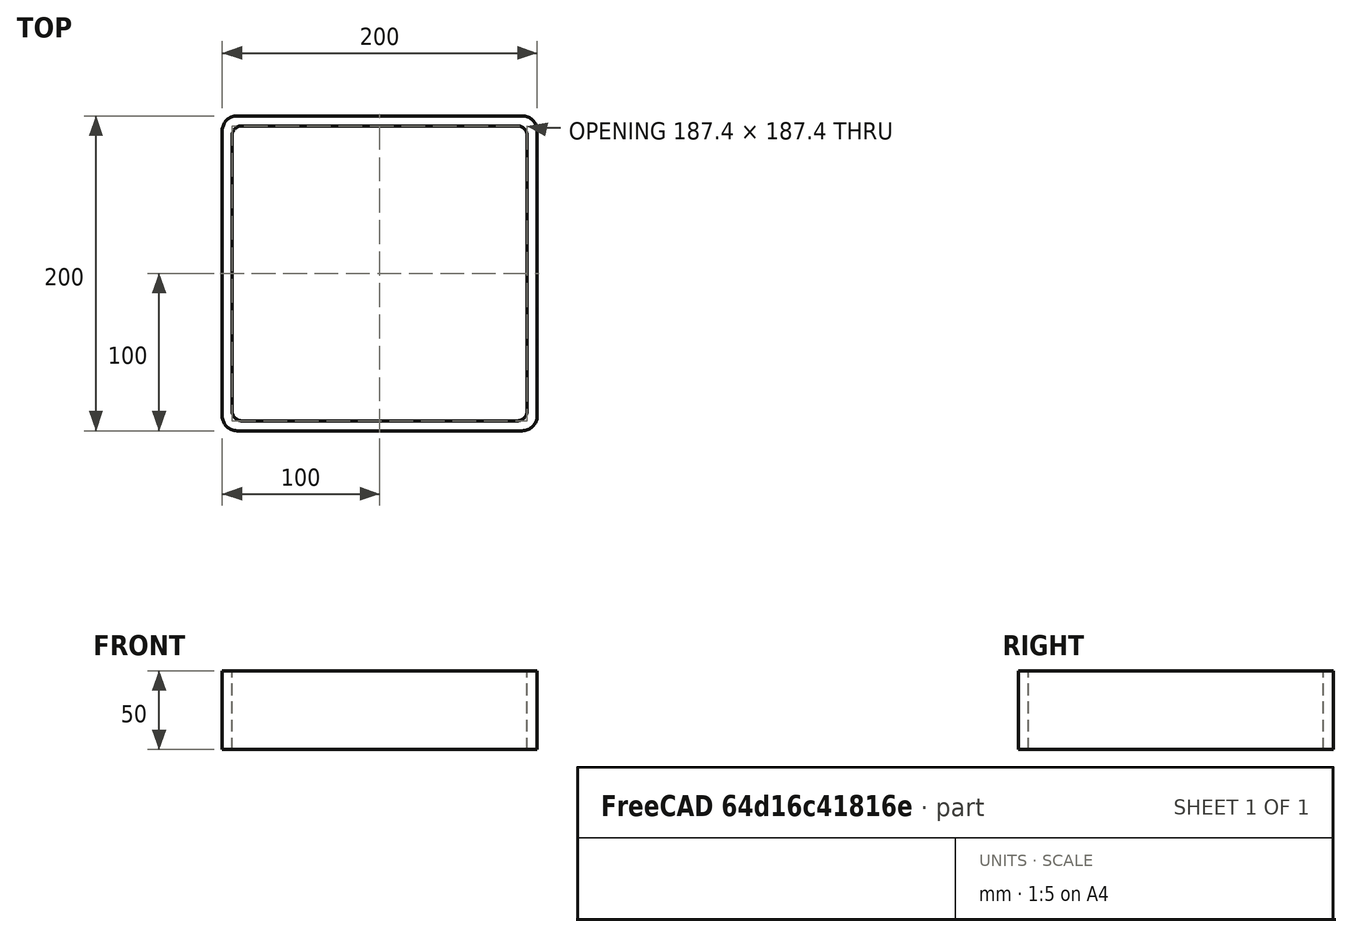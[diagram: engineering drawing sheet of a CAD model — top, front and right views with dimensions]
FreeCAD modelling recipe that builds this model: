
FCSTD DOCUMENT  (FreeCAD 0.15R4671 (Git))
Label: Square hollow section 200x200x6.3 EN10219 S235JRH
License: All rights reserved
LicenseURL: http://en.wikipedia.org/wiki/All_rights_reserved
objects: Sketcher::SketchObject×1, Part::Extrusion×1
note: 2 computed .brp shape members not serialized (recipe doc carries the construction recipe); baked Part::Feature solids carry a one-line shape summary decoded from their .brp

FEATURE [Sketcher::SketchObject] Sketch
  sketch-geometry (16):
    g0: LineSegment StartX=-87.4 StartY=93.7 StartZ=0 EndX=87.4 EndY=93.7 EndZ=0
    g1: LineSegment StartX=93.7 StartY=87.4 StartZ=0 EndX=93.7 EndY=-87.4 EndZ=0
    g2: LineSegment StartX=87.4 StartY=-93.7 StartZ=0 EndX=-87.4 EndY=-93.7 EndZ=0
    g3: LineSegment StartX=-93.7 StartY=-87.4 StartZ=0 EndX=-93.7 EndY=87.4 EndZ=0
    g4: LineSegment StartX=-90.55 StartY=100 StartZ=0 EndX=90.55 EndY=100 EndZ=0
    g5: LineSegment StartX=100 StartY=90.55 StartZ=0 EndX=100 EndY=-90.55 EndZ=0
    g6: LineSegment StartX=90.55 StartY=-100 StartZ=0 EndX=-90.55 EndY=-100 EndZ=0
    g7: LineSegment StartX=-100 StartY=-90.55 StartZ=0 EndX=-100 EndY=90.55 EndZ=0
    g8: ArcOfCircle CenterX=-87.4 CenterY=87.4 CenterZ=0 NormalX=0 NormalY=0 NormalZ=1 Radius=6.3 StartAngle=1.5708 EndAngle=3.14159
    g9: ArcOfCircle CenterX=87.4 CenterY=87.4 CenterZ=0 NormalX=0 NormalY=0 NormalZ=1 Radius=6.3 StartAngle=0 EndAngle=1.5708
    g10: ArcOfCircle CenterX=87.4 CenterY=-87.4 CenterZ=0 NormalX=0 NormalY=0 NormalZ=1 Radius=6.3 StartAngle=4.71239 EndAngle=6.28319
    g11: ArcOfCircle CenterX=-87.4 CenterY=-87.4 CenterZ=0 NormalX=0 NormalY=0 NormalZ=1 Radius=6.3 StartAngle=3.14159 EndAngle=4.71239
    g12: ArcOfCircle CenterX=90.55 CenterY=90.55 CenterZ=0 NormalX=0 NormalY=0 NormalZ=1 Radius=9.45 StartAngle=0 EndAngle=1.5708
    g13: ArcOfCircle CenterX=90.55 CenterY=-90.55 CenterZ=0 NormalX=0 NormalY=0 NormalZ=1 Radius=9.45 StartAngle=4.71239 EndAngle=6.28319
    g14: ArcOfCircle CenterX=-90.55 CenterY=-90.55 CenterZ=0 NormalX=0 NormalY=0 NormalZ=1 Radius=9.45 StartAngle=3.14159 EndAngle=4.71239
    g15: ArcOfCircle CenterX=-90.55 CenterY=90.55 CenterZ=0 NormalX=0 NormalY=0 NormalZ=1 Radius=9.45 StartAngle=1.5708 EndAngle=3.14159
  constraints (36):
    c: Horizontal(g2)
    c: Vertical(g3)
    c: Horizontal(g6)
    c: Vertical(g7)
    c: Tangent(g3,g8) = 1.5708
    c: Tangent(g0,g8) = 1.5708
    c: Tangent(g0,g9) = 1.5708
    c: Tangent(g1,g9) = 1.5708
    c: Tangent(g1,g10) = 1.5708
    c: Tangent(g2,g10) = 1.5708
    c: Tangent(g2,g11) = 1.5708
    c: Tangent(g3,g11) = 1.5708
    c: Tangent(g4,g12) = 1.5708
    c: Tangent(g5,g12) = 1.5708
    c: Tangent(g5,g13) = 1.5708
    c: Tangent(g6,g13) = 1.5708
    c: Tangent(g6,g14) = 1.5708
    c: Tangent(g7,g14) = 1.5708
    c: Tangent(g7,g15) = 1.5708
    c: Tangent(g4,g15) = 1.5708
    c: Equal(g9,g8)
    c: Equal(g9,g11)
    c: Equal(g9,g10)
    c: Equal(g12,g15)
    c: Equal(g12,g14)
    c: Equal(g12,g13)
    c: Symmetric(g4,g6,g-1)
    c: Symmetric(g7,g5,g-2)
    c: DistanceY(g4,g6) = -200
    c: DistanceX(g7,g5) = 200
    c: Symmetric(g3,g1,g-2)
    c: Symmetric(g0,g2,g-1)
    c: DistanceY(g0,g4) = 6.3
    c: DistanceX(g5,g1) = -6.3
    c: Radius(g9) = 6.3
    c: Radius(g12) = 9.45
FEATURE [Part::Extrusion] Extrude  label="Square hollow section 200x200x6.3 EN10219 S235JRH"
  Base = -> Sketch
  Dir = (0,0,50)
  Solid = true
